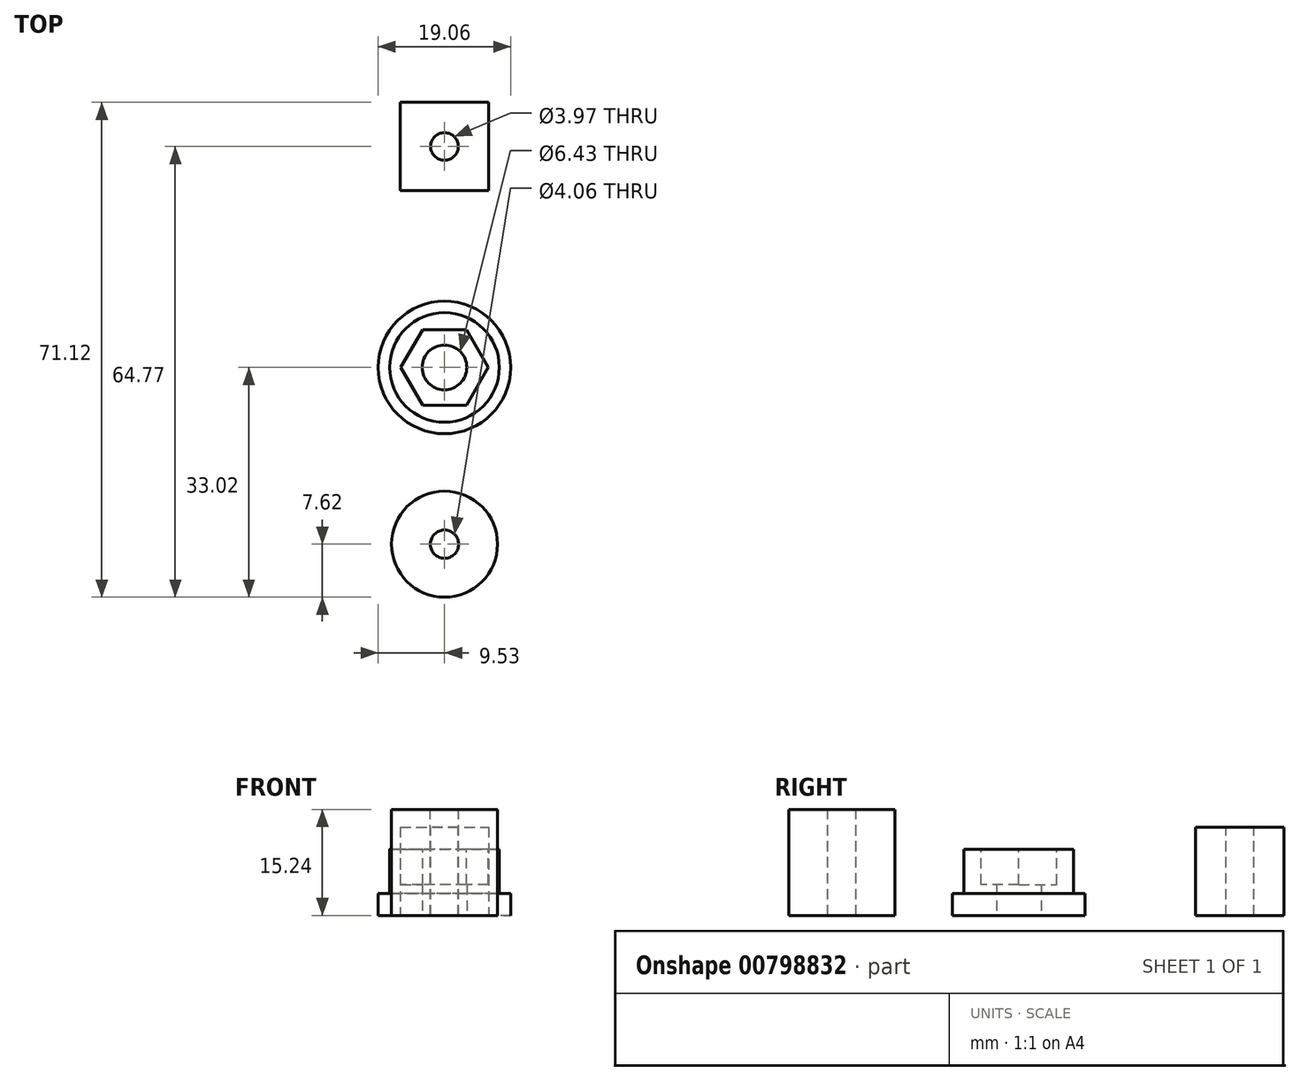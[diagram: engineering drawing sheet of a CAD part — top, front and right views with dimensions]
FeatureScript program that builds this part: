
annotation { "Feature Type Name" : "Feature", "Feature Type Description" : "" }
export const myFeature = defineFeature(function(context is Context, id is Id, definition is map)
    precondition{}
    {
        {
            var Q0;
            Q0=qCreatedBy(makeId("Top.planeOp"),FACE);
            var sketch = newSketch(context, id + "F0", { "sketchPlane" : qUnion([Q0])});
            skCircle(sketch, "E0", {"center": v(0, 0) * mm, "radius": 9.53 * mm});
            skSolve(sketch);
        }
        {
            var Q0;
            Q0 = qSketchRegion(id + "F0", true);
            extrude(context, id + "F1", {"entities" : qUnion([Q0]), "depth" : 3.17 * mm, "offsetDistance" : 25.4 * mm});
        }
        {
            var Q0;
            Q0=makeQuery(id+"F1.opExtrude","CAP_FACE",FACE,{"disambiguationData":[OSD([sQuery(id+"F0.wireOp",EDGE,"E0")])],"isStart":false});
            var sketch = newSketch(context, id + "F2", { "sketchPlane" : qUnion([Q0])});
            skCircle(sketch, "E1", {"center": v(0, 0) * mm, "radius": 7.87 * mm});
            skSolve(sketch);
        }
        {
            var Q0;
            Q0 = qSketchRegion(id + "F2", true);
            extrude(context, id + "F3", {"entities" : qUnion([Q0]), "operationType" : NewBodyOperationType.ADD, "depth" : 6.35 * mm, "offsetDistance" : 25.4 * mm});
        }
        {
            var Q0;
            Q0=makeQuery(id+"F3.opExtrude","CAP_FACE",FACE,{"disambiguationData":[OSD([sQuery(id+"F2.wireOp",EDGE,"E1")])],"isStart":false});
            var sketch = newSketch(context, id + "F4", { "sketchPlane" : qUnion([Q0])});
            skCircle(sketch, "E2", {"center": v(0, 0) * mm, "radius": 6.29 * mm, "construction": true});
            skLineSegment(sketch, "E3", {"start": v(0, 0) * mm, "end": v(3.14, 5.44) * mm, "construction": true});
            skLineSegment(sketch, "E4", {"start": v(0, 0) * mm, "end": v(-3.14, -5.44) * mm, "construction": true});
            skLineSegment(sketch, "E5", {"start": v(-3.14, 5.44) * mm, "end": v(0, 0) * mm, "construction": true});
            skLineSegment(sketch, "E6", {"start": v(0, 0) * mm, "end": v(3.14, -5.44) * mm, "construction": true});
            skLineSegment(sketch, "E7", {"start": v(3.14, 5.44) * mm, "end": v(-3.14, 5.44) * mm});
            skLineSegment(sketch, "E8", {"start": v(-3.14, 5.44) * mm, "end": v(-6.29, 0) * mm});
            skLineSegment(sketch, "E9", {"start": v(-6.29, 0) * mm, "end": v(-3.14, -5.44) * mm});
            skLineSegment(sketch, "E10", {"start": v(3.14, -5.44) * mm, "end": v(-3.14, -5.44) * mm});
            skLineSegment(sketch, "E11", {"start": v(3.14, -5.44) * mm, "end": v(6.29, 0) * mm});
            skLineSegment(sketch, "E12", {"start": v(6.29, 0) * mm, "end": v(3.14, 5.44) * mm});
            skSolve(sketch);
        }
        {
            var Q0;
            Q0 = qSketchRegion(id + "F4", true);
            extrude(context, id + "F5", {"entities" : qUnion([Q0]), "operationType" : NewBodyOperationType.REMOVE, "oppositeDirection" : true, "depth" : 5.08 * mm, "offsetDistance" : 25.4 * mm});
        }
        {
            var Q0;
            Q0=makeQuery(id+"F1.opExtrude","CAP_FACE",FACE,{"disambiguationData":[OSD([sQuery(id+"F0.wireOp",EDGE,"E0")])],"isStart":true});
            var sketch = newSketch(context, id + "F6", { "sketchPlane" : qUnion([Q0])});
            skCircle(sketch, "E13", {"center": v(0, 0) * mm, "radius": 3.21 * mm});
            skSolve(sketch);
        }
        {
            var Q0;
            Q0 = qSketchRegion(id + "F6", true);
            extrude(context, id + "F7", {"entities" : qUnion([Q0]), "operationType" : NewBodyOperationType.REMOVE, "endBound" : BoundingType.THROUGH_ALL, "oppositeDirection" : true, "depth" : 25.4 * mm, "offsetDistance" : 25.4 * mm});
        }
        {
            var Q0;
            Q0=qCreatedBy(makeId("Top.planeOp"),FACE);
            var sketch = newSketch(context, id + "F8", { "sketchPlane" : qUnion([Q0])});
            skLineSegment(sketch, "E14.bottom", {"start": v(-6.35, 38.1) * mm, "end": v(6.35, 38.1) * mm});
            skLineSegment(sketch, "E14.top", {"start": v(-6.35, 25.4) * mm, "end": v(6.35, 25.4) * mm});
            skLineSegment(sketch, "E14.left", {"start": v(-6.35, 38.1) * mm, "end": v(-6.35, 25.4) * mm});
            skLineSegment(sketch, "E14.right", {"start": v(6.35, 38.1) * mm, "end": v(6.35, 25.4) * mm});
            skSolve(sketch);
        }
        {
            var Q0;
            Q0 = qSketchRegion(id + "F8", true);
            extrude(context, id + "F9", {"entities" : qUnion([Q0]), "depth" : 12.7 * mm, "offsetDistance" : 25.4 * mm});
        }
        {
            var Q0;
            Q0=makeQuery(id+"F9.opExtrude","CAP_FACE",FACE,{"disambiguationData":[OSD([sQuery(id+"F8.wireOp",EDGE,"E14.bottom"),sQuery(id+"F8.wireOp",EDGE,"E14.top"),sQuery(id+"F8.wireOp",EDGE,"E14.left"),sQuery(id+"F8.wireOp",EDGE,"E14.right")])],"isStart":false});
            var sketch = newSketch(context, id + "F10", { "sketchPlane" : qUnion([Q0])});
            skCircle(sketch, "E15", {"center": v(0, 31.75) * mm, "radius": 1.99 * mm});
            skSolve(sketch);
        }
        {
            var Q0;
            Q0 = qSketchRegion(id + "F10", true);
            extrude(context, id + "F11", {"entities" : qUnion([Q0]), "operationType" : NewBodyOperationType.REMOVE, "endBound" : BoundingType.THROUGH_ALL, "oppositeDirection" : true, "depth" : 25.4 * mm, "offsetDistance" : 25.4 * mm});
        }
        {
            var Q0;
            Q0=qCreatedBy(makeId("Top.planeOp"),FACE);
            var sketch = newSketch(context, id + "F12", { "sketchPlane" : qUnion([Q0])});
            skCircle(sketch, "E16", {"center": v(0, -25.4) * mm, "radius": 7.62 * mm});
            skSolve(sketch);
        }
        {
            var Q0;
            Q0 = qSketchRegion(id + "F12", true);
            extrude(context, id + "F13", {"entities" : qUnion([Q0]), "depth" : 15.24 * mm, "offsetDistance" : 25.4 * mm});
        }
        {
            var Q0;
            Q0=makeQuery(id+"F13.opExtrude","CAP_FACE",FACE,{"disambiguationData":[OSD([sQuery(id+"F12.wireOp",EDGE,"E16")])],"isStart":false});
            var sketch = newSketch(context, id + "F14", { "sketchPlane" : qUnion([Q0])});
            skCircle(sketch, "E17", {"center": v(0, -25.4) * mm, "radius": 2.03 * mm});
            skSolve(sketch);
        }
        {
            var Q0;
            Q0 = qSketchRegion(id + "F14", true);
            extrude(context, id + "F15", {"entities" : qUnion([Q0]), "operationType" : NewBodyOperationType.REMOVE, "endBound" : BoundingType.THROUGH_ALL, "oppositeDirection" : true, "depth" : 25.4 * mm, "offsetDistance" : 25.4 * mm});
        }
    });
